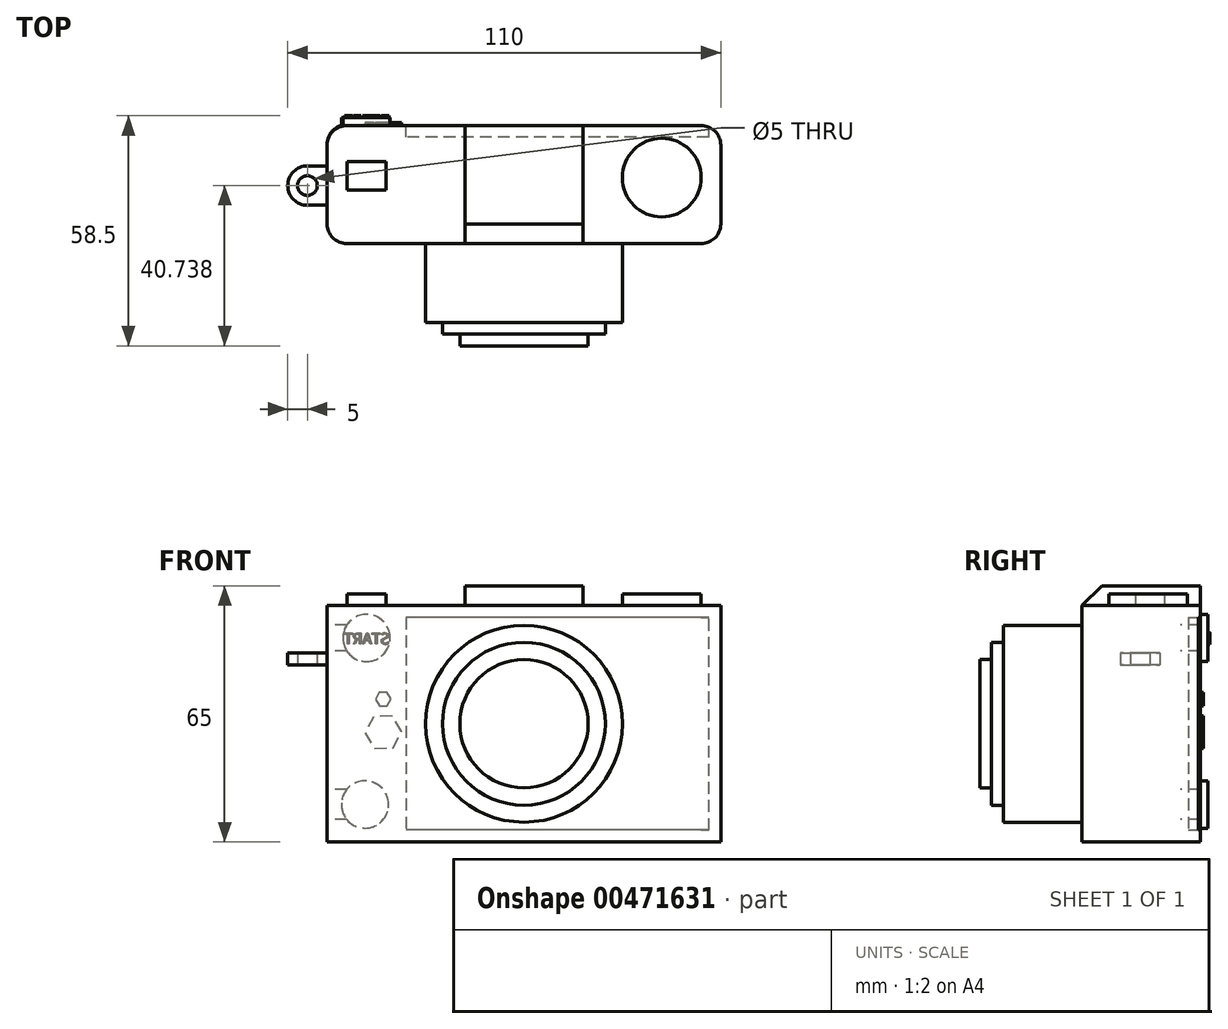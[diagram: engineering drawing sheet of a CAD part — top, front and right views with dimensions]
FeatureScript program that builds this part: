
annotation { "Feature Type Name" : "Feature", "Feature Type Description" : "" }
export const myFeature = defineFeature(function(context is Context, id is Id, definition is map)
    precondition{}
    {
        {
            var Q0;
            Q0=qCreatedBy(makeId("Front.planeOp"),FACE);
            var sketch = newSketch(context, id + "F0", { "sketchPlane" : qUnion([Q0])});
            skLineSegment(sketch, "E0.bottom", {"start": v(50, 30) * mm, "end": v(-50, 30) * mm});
            skLineSegment(sketch, "E0.top", {"start": v(50, -30) * mm, "end": v(-50, -30) * mm});
            skLineSegment(sketch, "E0.left", {"start": v(50, 30) * mm, "end": v(50, -30) * mm});
            skLineSegment(sketch, "E0.right", {"start": v(-50, 30) * mm, "end": v(-50, -30) * mm});
            skPoint(sketch, "E0.middle", {"position": v(0, 0) * mm});
            skSolve(sketch);
        }
        {
            var Q0;
            Q0=makeQuery(id+"F0.imprint","IMPRINT",FACE,{"disambiguationData":[TD([[makeQuery(id+"F0.imprint","IMPRINT",EDGE,{"derivedFrom":sQuery(id+"F0.wireOp",EDGE,"E0.bottom")}),1.0]])]});
            extrude(context, id + "F1", {"entities" : qUnion([Q0]), "depth" : 30 * mm});
        }
        {
            var Q0;
            Q0=makeQuery(id+"F1.opExtrude","CAP_FACE",FACE,{"disambiguationData":[OSD([sQuery(id+"F0.wireOp",EDGE,"E0.bottom"),sQuery(id+"F0.wireOp",EDGE,"E0.top"),sQuery(id+"F0.wireOp",EDGE,"E0.left"),sQuery(id+"F0.wireOp",EDGE,"E0.right")])],"isStart":false});
            var sketch = newSketch(context, id + "F2", { "sketchPlane" : qUnion([Q0])});
            skCircle(sketch, "E1", {"center": v(0, 0) * mm, "radius": 25 * mm});
            skSolve(sketch);
        }
        {
            var Q0;
            Q0=makeQuery(id+"F2.imprint","IMPRINT",FACE,{"disambiguationData":[TD([[makeQuery(id+"F2.imprint","IMPRINT",EDGE,{"derivedFrom":sQuery(id+"F2.wireOp",EDGE,"E1")}),1.0]])]});
            extrude(context, id + "F3", {"entities" : qUnion([Q0]), "operationType" : NewBodyOperationType.ADD, "depth" : 20 * mm});
        }
        {
            var Q0;
            Q0=makeQuery(id+"F1.opExtrude","SWEPT_FACE",FACE,{"disambiguationData":[OSD([sQuery(id+"F0.wireOp",EDGE,"E0.bottom")])]});
            var sketch = newSketch(context, id + "F4", { "sketchPlane" : qUnion([Q0])});
            skCircle(sketch, "E2", {"center": v(35, -13.23) * mm, "radius": 10 * mm});
            skSolve(sketch);
        }
        {
            var Q0;
            Q0=makeQuery(id+"F4.imprint","IMPRINT",FACE,{"disambiguationData":[TD([[makeQuery(id+"F4.imprint","IMPRINT",EDGE,{"derivedFrom":sQuery(id+"F4.wireOp",EDGE,"E2")}),1.0]])]});
            extrude(context, id + "F5", {"entities" : qUnion([Q0]), "operationType" : NewBodyOperationType.ADD, "depth" : 3 * mm});
        }
        {
            var Q0;
            Q0=makeQuery(id+"F1.opExtrude","SWEPT_FACE",FACE,{"disambiguationData":[OSD([sQuery(id+"F0.wireOp",EDGE,"E0.bottom")])]});
            var sketch = newSketch(context, id + "F6", { "sketchPlane" : qUnion([Q0])});
            skLineSegment(sketch, "E3.bottom", {"start": v(-35, -16.43) * mm, "end": v(-44.97, -16.43) * mm});
            skLineSegment(sketch, "E3.top", {"start": v(-35, -9.15) * mm, "end": v(-44.97, -9.15) * mm});
            skLineSegment(sketch, "E3.left", {"start": v(-35, -16.43) * mm, "end": v(-35, -9.15) * mm});
            skLineSegment(sketch, "E3.right", {"start": v(-44.97, -16.43) * mm, "end": v(-44.97, -9.15) * mm});
            skPoint(sketch, "E3.middle", {"position": v(-39.99, -12.8) * mm});
            skSolve(sketch);
        }
        {
            var Q0;
            Q0=makeQuery(id+"F6.imprint","IMPRINT",FACE,{"disambiguationData":[TD([[makeQuery(id+"F6.imprint","IMPRINT",EDGE,{"derivedFrom":sQuery(id+"F6.wireOp",EDGE,"E3.bottom")}),-1.0]])]});
            extrude(context, id + "F7", {"entities" : qUnion([Q0]), "operationType" : NewBodyOperationType.ADD, "depth" : 3 * mm});
        }
        {
            var Q0;
            Q0=makeQuery(id+"F1.opExtrude","SWEPT_FACE",FACE,{"disambiguationData":[OSD([sQuery(id+"F0.wireOp",EDGE,"E0.bottom")])]});
            var sketch = newSketch(context, id + "F8", { "sketchPlane" : qUnion([Q0])});
            skLineSegment(sketch, "E4.bottom", {"start": v(15, 0) * mm, "end": v(-15, 0) * mm});
            skLineSegment(sketch, "E4.top", {"start": v(15, -30) * mm, "end": v(-15, -30) * mm});
            skLineSegment(sketch, "E4.left", {"start": v(15, 0) * mm, "end": v(15, -30) * mm});
            skLineSegment(sketch, "E4.right", {"start": v(-15, 0) * mm, "end": v(-15, -30) * mm});
            skPoint(sketch, "E4.middle", {"position": v(0, -15) * mm});
            skSolve(sketch);
        }
        {
            var Q0;
            Q0=makeQuery(id+"F8.imprint","IMPRINT",FACE,{"disambiguationData":[TD([[makeQuery(id+"F8.imprint","IMPRINT",EDGE,{"derivedFrom":sQuery(id+"F8.wireOp",EDGE,"E4.bottom")}),1.0]])]});
            extrude(context, id + "F9", {"entities" : qUnion([Q0]), "operationType" : NewBodyOperationType.ADD, "depth" : 5 * mm});
        }
        {
            var Q0;
            Q0=makeQuery(id+"F9.opExtrude","SWEPT_FACE",FACE,{"disambiguationData":[OSD([sQuery(id+"F8.wireOp",EDGE,"E4.left")])]});
            var sketch = newSketch(context, id + "F10", { "sketchPlane" : qUnion([Q0])});
            skLineSegment(sketch, "E5", {"start": v(-30, 30) * mm, "end": v(-25, 35) * mm});
            skSolve(sketch);
        }
        {
            var Q0;
            {var subQ0=sQuery(id+"F10.wireOp",EDGE,"E5");Q0=makeQuery(id+"F10.imprint","IMPRINT",FACE,{"disambiguationData":[TD([[makeQuery(id+"F10.imprint","IMPRINT",EDGE,{"derivedFrom":subQ0}),1.0]])]});}
            extrude(context, id + "F11", {"entities" : qUnion([Q0]), "operationType" : NewBodyOperationType.REMOVE, "oppositeDirection" : true, "depth" : 25 * mm});
        }
        {
            var Q0;
            Q0=makeQuery(id+"F9.opExtrude","SWEPT_FACE",FACE,{"disambiguationData":[OSD([sQuery(id+"F8.wireOp",EDGE,"E4.right")])]});
            var sketch = newSketch(context, id + "F12", { "sketchPlane" : qUnion([Q0])});
            skLineSegment(sketch, "E6", {"start": v(30, 30) * mm, "end": v(25, 35) * mm});
            skSolve(sketch);
        }
        {
            var Q0;
            {var subQ0=sQuery(id+"F12.wireOp",EDGE,"E6");Q0=makeQuery(id+"F12.imprint","IMPRINT",FACE,{"disambiguationData":[TD([[makeQuery(id+"F12.imprint","IMPRINT",EDGE,{"derivedFrom":subQ0}),-1.0]])]});}
            extrude(context, id + "F13", {"entities" : qUnion([Q0]), "operationType" : NewBodyOperationType.REMOVE, "oppositeDirection" : true, "depth" : 25 * mm});
        }
        {
            var Q0;
            Q0=qCreatedBy(makeId("Front.planeOp"),FACE);
            var sketch = newSketch(context, id + "F14", { "sketchPlane" : qUnion([Q0])});
            skLineSegment(sketch, "E7.bottom", {"start": v(47, 27) * mm, "end": v(-30, 27) * mm});
            skLineSegment(sketch, "E7.top", {"start": v(47, -27) * mm, "end": v(-30, -27) * mm});
            skLineSegment(sketch, "E7.left", {"start": v(47, 27) * mm, "end": v(47, -27) * mm});
            skLineSegment(sketch, "E7.right", {"start": v(-30, 27) * mm, "end": v(-30, -27) * mm});
            skSolve(sketch);
        }
        {
            var Q0;
            Q0=makeQuery(id+"F14.imprint","IMPRINT",FACE,{"disambiguationData":[TD([[makeQuery(id+"F14.imprint","IMPRINT",EDGE,{"derivedFrom":sQuery(id+"F14.wireOp",EDGE,"E7.bottom")}),1.0]])]});
            extrude(context, id + "F15", {"entities" : qUnion([Q0]), "operationType" : NewBodyOperationType.REMOVE, "depth" : 3 * mm});
        }
        {
            var Q0;
            Q0=qCreatedBy(makeId("Front.planeOp"),FACE);
            var sketch = newSketch(context, id + "F16", { "sketchPlane" : qUnion([Q0])});
            skCircle(sketch, "E8", {"center": v(-40, 21.8) * mm, "radius": 6 * mm});
            skCircle(sketch, "E9", {"center": v(-40.38, -20.52) * mm, "radius": 6 * mm});
            skSolve(sketch);
        }
        {
            var Q0;
            Q0=makeQuery(id+"F16.imprint","IMPRINT",FACE,{"disambiguationData":[TD([[makeQuery(id+"F16.imprint","IMPRINT",EDGE,{"derivedFrom":sQuery(id+"F16.wireOp",EDGE,"E8")}),1.0]])]});
            var Q1;
            Q1=makeQuery(id+"F16.imprint","IMPRINT",FACE,{"disambiguationData":[TD([[makeQuery(id+"F16.imprint","IMPRINT",EDGE,{"derivedFrom":sQuery(id+"F16.wireOp",EDGE,"E9")}),1.0]])]});
            extrude(context, id + "F17", {"entities" : qUnion([Q0, Q1]), "operationType" : NewBodyOperationType.ADD, "oppositeDirection" : true, "depth" : 2 * mm});
        }
        {
            var Q0;
            Q0=makeQuery(id+"F1.opExtrude","CAP_EDGE",EDGE,{"disambiguationData":[OSD([sQuery(id+"F0.wireOp",EDGE,"E0.left")])],"isStart":true});
            var Q1;
            Q1=makeQuery(id+"F1.opExtrude","CAP_EDGE",EDGE,{"disambiguationData":[OSD([sQuery(id+"F0.wireOp",EDGE,"E0.right")])],"isStart":true});
            fillet(context, id + "F18", {"entities" : qUnion([Q0, Q1]), "radius" : 5 * mm, "tangentPropagation" : true, "allowEdgeOverflow" : false});
        }
        {
            var Q0;
            Q0=makeQuery(id+"F1.opExtrude","CAP_EDGE",EDGE,{"disambiguationData":[OSD([sQuery(id+"F0.wireOp",EDGE,"E0.right")])],"isStart":false});
            fillet(context, id + "F19", {"entities" : qUnion([Q0]), "radius" : 5 * mm, "tangentPropagation" : true, "allowEdgeOverflow" : false});
        }
        {
            var Q0;
            Q0=makeQuery(id+"F1.opExtrude","CAP_EDGE",EDGE,{"disambiguationData":[OSD([sQuery(id+"F0.wireOp",EDGE,"E0.left")])],"isStart":false});
            fillet(context, id + "F20", {"entities" : qUnion([Q0]), "radius" : 5 * mm, "tangentPropagation" : true, "allowEdgeOverflow" : false});
        }
        {
            var Q0;
            Q0=makeQuery(id+"F15.boolean.opBoolean","COPY",FACE,{"derivedFrom":makeQuery(id+"F15.opExtrude","CAP_FACE",FACE,{"disambiguationData":[OSD([sQuery(id+"F14.wireOp",EDGE,"E7.bottom"),sQuery(id+"F14.wireOp",EDGE,"E7.top"),sQuery(id+"F14.wireOp",EDGE,"E7.left"),sQuery(id+"F14.wireOp",EDGE,"E7.right")])],"isStart":false})});
            var sketch = newSketch(context, id + "F21", { "sketchPlane" : qUnion([Q0])});
            skCircle(sketch, "E10.cCircle", {"center": v(35.74, -2.16) * mm, "radius": 4.05 * mm, "construction": true});
            skLineSegment(sketch, "E10.0", {"start": v(31.07, -1.98) * mm, "end": v(33.56, 1.98) * mm});
            skLineSegment(sketch, "E10.1", {"start": v(33.56, 1.98) * mm, "end": v(38.23, 1.8) * mm});
            skLineSegment(sketch, "E10.2", {"start": v(38.23, 1.8) * mm, "end": v(40.4, -2.34) * mm});
            skLineSegment(sketch, "E10.3", {"start": v(40.4, -2.34) * mm, "end": v(37.91, -6.3) * mm});
            skLineSegment(sketch, "E10.4", {"start": v(37.91, -6.3) * mm, "end": v(33.24, -6.11) * mm});
            skLineSegment(sketch, "E10.5", {"start": v(33.24, -6.11) * mm, "end": v(31.07, -1.98) * mm});
            skPoint(sketch, "E10.0.midPoint", {"position": v(32.32, 0) * mm});
            skCircle(sketch, "E11.cCircle", {"center": v(35.74, 6.25) * mm, "radius": 1.73 * mm, "construction": true});
            skLineSegment(sketch, "E11.0", {"start": v(37.73, 6.22) * mm, "end": v(36.71, 4.5) * mm});
            skLineSegment(sketch, "E11.1", {"start": v(36.71, 4.5) * mm, "end": v(34.72, 4.54) * mm});
            skLineSegment(sketch, "E11.2", {"start": v(34.72, 4.54) * mm, "end": v(33.75, 6.28) * mm});
            skLineSegment(sketch, "E11.3", {"start": v(33.75, 6.28) * mm, "end": v(34.77, 7.99) * mm});
            skLineSegment(sketch, "E11.4", {"start": v(34.77, 7.99) * mm, "end": v(36.76, 7.96) * mm});
            skLineSegment(sketch, "E11.5", {"start": v(36.76, 7.96) * mm, "end": v(37.73, 6.22) * mm});
            skPoint(sketch, "E11.0.midPoint", {"position": v(37.22, 5.37) * mm});
            skSolve(sketch);
        }
        {
            var Q0;
            Q0 = qSketchRegion(id + "F21", true);
            extrude(context, id + "F22", {"entities" : qUnion([Q0]), "operationType" : NewBodyOperationType.ADD, "depth" : 3.8 * mm});
        }
        {
            var Q0;
            Q0=makeQuery(id+"F17.opExtrude","CAP_FACE",FACE,{"disambiguationData":[OSD([sQuery(id+"F16.wireOp",EDGE,"E8")])],"isStart":false});
            var sketch = newSketch(context, id + "F23", { "sketchPlane" : qUnion([Q0])});
            skText(sketch, "E12", { "text": "START", "fontName": "NotoSansCJKkr-Regular.otf"});
            const initialGuessF23  = {"E12": [0.03412, 0.02023, 1, 0, 0.00275]};
            skSetInitialGuess(sketch, initialGuessF23);
            skSolve(sketch);
        }
        {
            var Q0;
            Q0 = qSketchRegion(id + "F23", true);
            extrude(context, id + "F24", {"entities" : qUnion([Q0]), "operationType" : NewBodyOperationType.ADD, "depth" : 0.5 * mm});
        }
        {
            var Q0;
            Q0=qCreatedBy(makeId("Front.planeOp"),FACE);
            var sketch = newSketch(context, id + "F25", { "sketchPlane" : qUnion([Q0])});
            skText(sketch, "E13", { "text": "SSSB", "fontName": "AllertaStencil-Regular.ttf"});
            const initialGuessF25  = {"E13": [-0.0066, 0.03023, 1, 0, 0.0041]};
            skSetInitialGuess(sketch, initialGuessF25);
            skSolve(sketch);
        }
        {
            var Q0;
            Q0 = qSketchRegion(id + "F25", true);
            extrude(context, id + "F26", {"entities" : qUnion([Q0]), "operationType" : NewBodyOperationType.ADD, "depth" : 25 * mm});
        }
        {
            var Q0;
            Q0=makeQuery(id+"F3.opExtrude","CAP_FACE",FACE,{"disambiguationData":[OSD([sQuery(id+"F2.wireOp",EDGE,"E1")])],"isStart":false});
            var sketch = newSketch(context, id + "F27", { "sketchPlane" : qUnion([Q0])});
            skCircle(sketch, "E14", {"center": v(0, 0) * mm, "radius": 20.68 * mm});
            skSolve(sketch);
        }
        {
            var Q0;
            Q0=makeQuery(id+"F27.imprint","IMPRINT",FACE,{"disambiguationData":[TD([[makeQuery(id+"F27.imprint","IMPRINT",EDGE,{"derivedFrom":sQuery(id+"F27.wireOp",EDGE,"E14")}),1.0]])]});
            extrude(context, id + "F28", {"entities" : qUnion([Q0]), "operationType" : NewBodyOperationType.ADD, "depth" : 3 * mm, "offsetDistance" : 25 * mm});
        }
        {
            var Q0;
            Q0=makeQuery(id+"F28.opExtrude","CAP_FACE",FACE,{"disambiguationData":[OSD([sQuery(id+"F27.wireOp",EDGE,"E14")])],"isStart":false});
            var sketch = newSketch(context, id + "F29", { "sketchPlane" : qUnion([Q0])});
            skCircle(sketch, "E15", {"center": v(0, 0) * mm, "radius": 16.3 * mm});
            skSolve(sketch);
        }
        {
            var Q0;
            Q0=makeQuery(id+"F29.imprint","IMPRINT",FACE,{"disambiguationData":[TD([[makeQuery(id+"F29.imprint","IMPRINT",EDGE,{"derivedFrom":sQuery(id+"F29.wireOp",EDGE,"E15")}),1.0]])]});
            extrude(context, id + "F30", {"entities" : qUnion([Q0]), "operationType" : NewBodyOperationType.ADD, "depth" : 3 * mm, "offsetDistance" : 25 * mm});
        }
        {
            var Q0;
            {var subQ0=sQuery(id+"F0.wireOp",EDGE,"E0.right");var subQ3=sQuery(id+"F0.wireOp",EDGE,"E0.bottom");Q0=makeQuery(id+"F9.boolean.opBoolean","SPLIT",FACE,{"disambiguationData":[TD([makeQuery(id+"F1.opExtrude","SWEPT_FACE",FACE,{"disambiguationData":[OSD([subQ0])]})])],"derivedFrom":makeQuery(id+"F1.opExtrude","SWEPT_FACE",FACE,{"disambiguationData":[OSD([subQ3])]})});}
            cPlane(context, id + "F31", {"entities" : qUnion([Q0]), "cplaneType" : CPlaneType.OFFSET, "offset" : 15 * mm, "oppositeDirection" : true, "width" : 150 * mm, "height" : 150 * mm});
        }
        {
            var Q0;
            Q0=qCreatedBy(id+"F31.planeOp",FACE);
            var sketch = newSketch(context, id + "F32", { "sketchPlane" : qUnion([Q0])});
            skArc(sketch, "E16", {"start": v(-55, -10.26) * mm, "mid": v(-60, -15.26) * mm, "end": v(-55, -20.26) * mm});
            skCircle(sketch, "E17", {"center": v(-55, -15.26) * mm, "radius": 2.5 * mm});
            skLineSegment(sketch, "E18", {"start": v(-55, -20.26) * mm, "end": v(-50, -20.26) * mm});
            skLineSegment(sketch, "E19", {"start": v(-55, -10.26) * mm, "end": v(-50, -10.26) * mm});
            skLineSegment(sketch, "E20", {"start": v(-50, -20.26) * mm, "end": v(-50, -10.26) * mm});
            skSolve(sketch);
        }
        {
            var Q0;
            Q0 = qSketchRegion(id + "F32", true);
            extrude(context, id + "F33", {"entities" : qUnion([Q0]), "operationType" : NewBodyOperationType.ADD, "depth" : 3 * mm, "offsetDistance" : 25 * mm});
        }
    });
